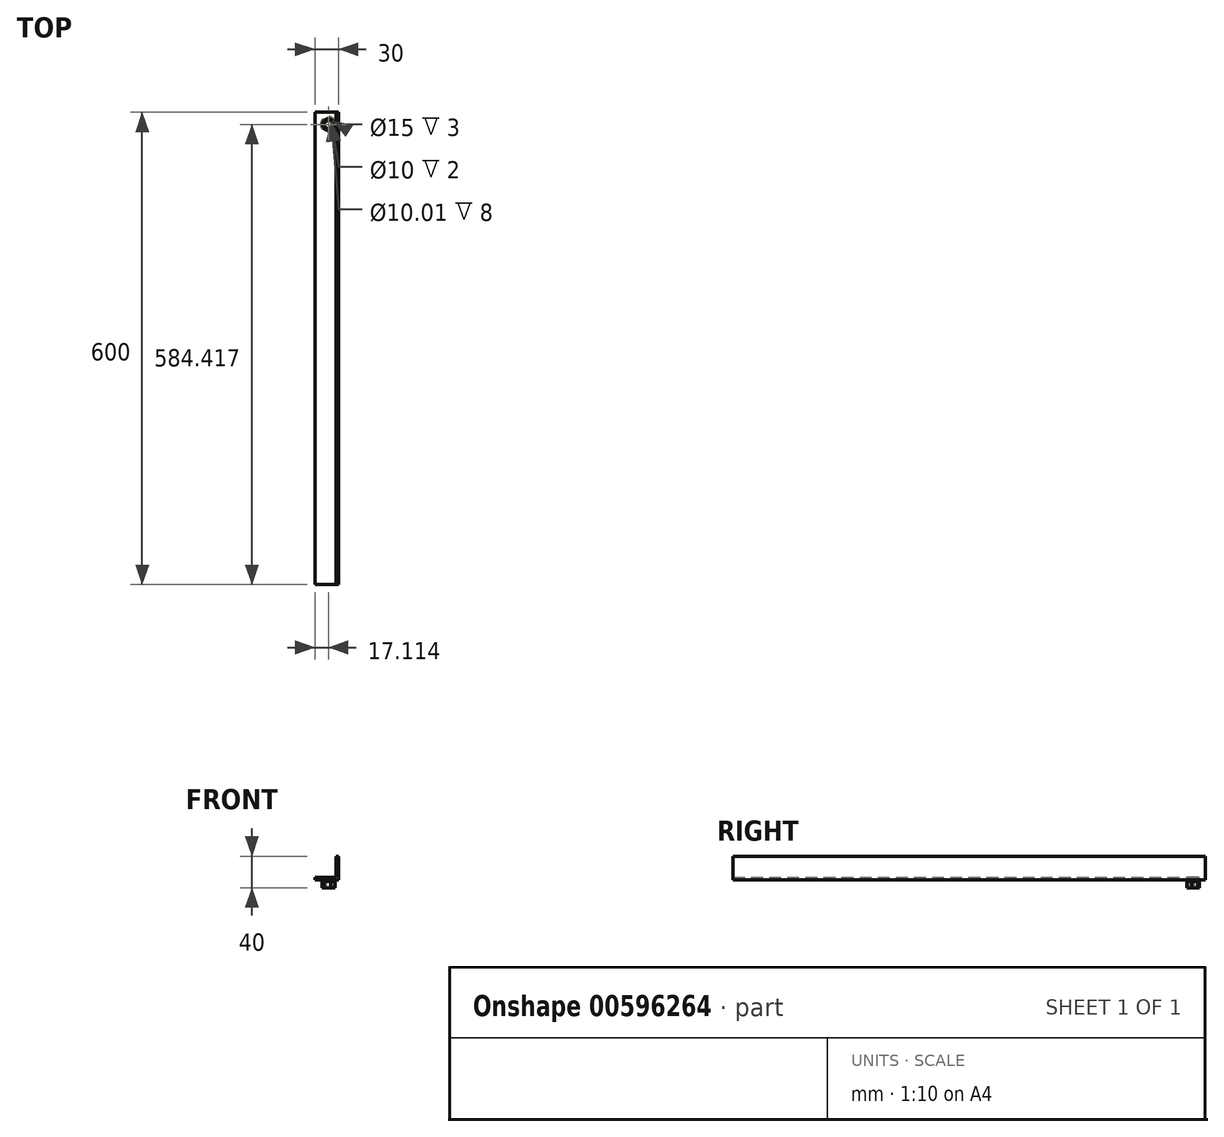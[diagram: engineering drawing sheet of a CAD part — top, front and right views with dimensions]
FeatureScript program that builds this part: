
annotation { "Feature Type Name" : "Feature", "Feature Type Description" : "" }
export const myFeature = defineFeature(function(context is Context, id is Id, definition is map)
    precondition{}
    {
        {
            var Q0;
            Q0=qCreatedBy(makeId("Front.planeOp"),FACE);
            var sketch = newSketch(context, id + "F0", { "sketchPlane" : qUnion([Q0])});
            skLineSegment(sketch, "E0", {"start": v(-30, 0) * mm, "end": v(0, 0) * mm, "construction": true});
            skLineSegment(sketch, "E1", {"start": v(0, 0) * mm, "end": v(0, 30) * mm});
            skLineSegment(sketch, "E2", {"start": v(0, 30) * mm, "end": v(-3, 30) * mm});
            skLineSegment(sketch, "E3", {"start": v(-3, 30) * mm, "end": v(-3, 3) * mm});
            skLineSegment(sketch, "E4", {"start": v(-3, 3) * mm, "end": v(-30, 3) * mm});
            skLineSegment(sketch, "E5", {"start": v(-30, 3) * mm, "end": v(-30, 0) * mm});
            skLineSegment(sketch, "E6", {"start": v(0, 0) * mm, "end": v(-30, 0) * mm});
            skSolve(sketch);
        }
        {
            var Q0;
            Q0 = qSketchRegion(id + "F0", true);
            extrude(context, id + "F1", {"entities" : qUnion([Q0]), "depth" : 600 * mm, "offsetDistance" : 25 * mm});
        }
        {
            var Q0;
            Q0=makeQuery(id+"F1.opExtrude","SWEPT_FACE",FACE,{"disambiguationData":[OSD([sQuery(id+"F0.wireOp",EDGE,"E6")])]});
            var sketch = newSketch(context, id + "F2", { "sketchPlane" : qUnion([Q0])});
            skCircle(sketch, "E7", {"center": v(-12.89, 15.58) * mm, "radius": 7.5 * mm});
            skSolve(sketch);
        }
        {
            var Q0;
            Q0=makeQuery(id+"F2.imprint","IMPRINT",FACE,{"disambiguationData":[TD([[makeQuery(id+"F2.imprint","IMPRINT",EDGE,{"derivedFrom":sQuery(id+"F2.wireOp",EDGE,"E7")}),1.0]])]});
            extrude(context, id + "F3", {"entities" : qUnion([Q0]), "operationType" : NewBodyOperationType.REMOVE, "oppositeDirection" : true, "depth" : 25 * mm, "offsetDistance" : 25 * mm});
        }
        {
            var Q0;
            Q0=makeQuery(id+"F1.opExtrude","SWEPT_FACE",FACE,{"disambiguationData":[OSD([sQuery(id+"F0.wireOp",EDGE,"E6")])]});
            var sketch = newSketch(context, id + "F4", { "sketchPlane" : qUnion([Q0])});
            skCircle(sketch, "E8.0", {"center": v(-12.89, 15.58) * mm, "radius": 7.5 * mm, "construction": true});
            skCircle(sketch, "E9", {"center": v(-12.89, 15.58) * mm, "radius": 5 * mm});
            skCircle(sketch, "E10", {"center": v(-12.89, 15.58) * mm, "radius": 10 * mm});
            skSolve(sketch);
        }
        {
            var Q0;
            Q0 = qSketchRegion(id + "F4", true);
            extrude(context, id + "F5", {"entities" : qUnion([Q0]), "operationType" : NewBodyOperationType.ADD, "depth" : 2 * mm, "offsetDistance" : 25 * mm});
        }
        {
            var Q0;
            Q0=makeQuery(id+"F5.opExtrude","CAP_FACE",FACE,{"disambiguationData":[OSD([sQuery(id+"F4.wireOp",EDGE,"E9"),sQuery(id+"F4.wireOp",EDGE,"E10")])],"isStart":false});
            var sketch = newSketch(context, id + "F6", { "sketchPlane" : qUnion([Q0])});
            skCircle(sketch, "E11.0", {"center": v(-12.89, 15.58) * mm, "radius": 5 * mm, "construction": true});
            skCircle(sketch, "E12", {"center": v(-12.89, 15.58) * mm, "radius": 5 * mm});
            skCircle(sketch, "E13", {"center": v(-12.89, 15.58) * mm, "radius": 7.35 * mm, "construction": true});
            skLineSegment(sketch, "E14.0", {"start": v(-10.28, 23.66) * mm, "end": v(-4.58, 17.37) * mm});
            skLineSegment(sketch, "E14.1", {"start": v(-4.58, 17.37) * mm, "end": v(-7.2, 9.28) * mm});
            skLineSegment(sketch, "E14.2", {"start": v(-7.2, 9.28) * mm, "end": v(-15.5, 7.5) * mm});
            skLineSegment(sketch, "E14.3", {"start": v(-15.5, 7.5) * mm, "end": v(-21.19, 13.8) * mm});
            skLineSegment(sketch, "E14.4", {"start": v(-21.19, 13.8) * mm, "end": v(-18.58, 21.88) * mm});
            skLineSegment(sketch, "E14.5", {"start": v(-18.58, 21.88) * mm, "end": v(-10.28, 23.66) * mm});
            skPoint(sketch, "E14.0.midPoint", {"position": v(-7.43, 20.51) * mm});
            skSolve(sketch);
        }
        {
            var Q0;
            Q0 = qSketchRegion(id + "F6", true);
            extrude(context, id + "F7", {"entities" : qUnion([Q0]), "operationType" : NewBodyOperationType.ADD, "depth" : 8 * mm, "offsetDistance" : 25 * mm});
        }
    });
